# Revit family: HVAC-Chilled_Beam-Dadanco-ACB30
name_source: partatom
category: Mechanical Equipment
revit_build: Autodesk Revit 2015 (Build: 20140903_1530(x64)
units: mm (PartAtom-declared; Revit-internal decimal feet)

## types (6) — shared parameters
Assembly Code = D3040100
Cooling Primary Air Dry Bulb = 55 °F
Cooling Primary Air Wet Bulb = 53 °F
Cooling Room Dry Bulb = 75 °F
Cooling Room Relative Humidity = 50
Default Elevation = 9' - 0"
Description = Active Chilled Beam
Drain material = <By Category>
Heating Primary Air Dry Bulb = 55 °F
Heating Room Dry Bulb = 70 °F
Height = 0' - 11 11/16"
Housing Material = Metal-Dadanco-Steel-Galvanized
Keynote = 23 37 00.A1
Manufacturer = Dadanco
Model = ACB30
SCHW Temperature = 57 °F
SHHW Temperature = 110 °F
Type Comments = 1 Way, Discharge Vertical Coil
URL = http://www.dadanco.com
Width = 0' - 8 25/32"

## per-type parameters (varying)
- ACB-1: 2 Pipe Coil Configuration=No; 2 or 4 pipe=4; CWF=2 GPM; CWPD=3.40 psi; Cooling Supply Air Temperature=58 °F; HWF=1 GPM; HWPD=0.32 psi; Heating Supply Air Temperature=91 °F; Latent Cooling=140.0 Btu/h; Length=2' - 0"; Net Unit Cooling Sensible=1731.0 Btu/h; Net Unit Heating Sensible=2209.0 Btu/h; Nominal Unit Length=2' - 0"; Nozzle Configuration=15-SN; PA=20 CFM; PASP=0.50 in-wg; Primary Air Inlet Size=0' - 4"; SCHW Temp Out=59 °F; SHHW Temp Out=99 °F; Secondary Air Sensible Cooling=1296.0 Btu/h; Secondary Air Sensible Heating=2535.0 Btu/h; Sound Level NC=15; Sound Level dBA=20; Supply Air=96 CFM; Total Cooling Capacity=1870.0 Btu/h
- ACB-2: 2 Pipe Coil Configuration=No; 2 or 4 pipe=4; CWF=1 GPM; CWPD=0.40 psi; Cooling Supply Air Temperature=61 °F; HWF=2 GPM; HWPD=1.08 psi; Heating Supply Air Temperature=87 °F; Latent Cooling=279.0 Btu/h; Length=2' - 8"; Net Unit Cooling Sensible=2427.0 Btu/h; Net Unit Heating Sensible=3071.0 Btu/h; Nominal Unit Length=3' - 0"; Nozzle Configuration=25-MN; PA=40 CFM; PASP=0.40 in-wg; Primary Air Inlet Size=0' - 4"; SCHW Temp Out=64 °F; SHHW Temp Out=105 °F; Secondary Air Sensible Cooling=1558.0 Btu/h; Secondary Air Sensible Heating=3722.0 Btu/h; Sound Level NC=15; Sound Level dBA=22; Supply Air=165 CFM; Total Cooling Capacity=2706.0 Btu/h
- ACB-3: 2 Pipe Coil Configuration=No; 2 or 4 pipe=4; CWF=1 GPM; CWPD=1.90 psi; Cooling Supply Air Temperature=61 °F; HWF=1 GPM; HWPD=0.48 psi; Heating Supply Air Temperature=86 °F; Latent Cooling=349.0 Btu/h; Length=3' - 4"; Net Unit Cooling Sensible=3261.0 Btu/h; Net Unit Heating Sensible=3576.0 Btu/h; Nominal Unit Length=4' - 0"; Nozzle Configuration=35-MN; PA=50 CFM; PASP=0.40 in-wg; Primary Air Inlet Size=0' - 6"; SCHW Temp Out=62 °F; SHHW Temp Out=99 °F; Secondary Air Sensible Cooling=2174.0 Btu/h; Secondary Air Sensible Heating=4391.0 Btu/h; Sound Level NC=16; Sound Level dBA=26; Supply Air=209 CFM; Total Cooling Capacity=3610.0 Btu/h
- ACB-4: 2 Pipe Coil Configuration=Yes; 2 or 4 pipe=2; CWF=1 GPM; CWPD=2.50 psi; Cooling Supply Air Temperature=60 °F; HWF=1 GPM; HWPD=4.56 psi; Heating Supply Air Temperature=92 °F; Latent Cooling=419.0 Btu/h; Length=4' - 4"; Net Unit Cooling Sensible=4351.0 Btu/h; Net Unit Heating Sensible=6173.0 Btu/h; Nominal Unit Length=5' - 0"; Nozzle Configuration=40-MN; PA=60 CFM; PASP=0.40 in-wg; Primary Air Inlet Size=0' - 6"; SCHW Temp Out=65 °F; SHHW Temp Out=97 °F; Secondary Air Sensible Cooling=3048.0 Btu/h; Secondary Air Sensible Heating=7151.0 Btu/h; Sound Level NC=19; Sound Level dBA=30; Supply Air=261 CFM; Total Cooling Capacity=4770.0 Btu/h
- ACB-5: 2 Pipe Coil Configuration=No; 2 or 4 pipe=4; CWF=1 GPM; CWPD=4.20 psi; Cooling Supply Air Temperature=61 °F; HWF=1 GPM; HWPD=1.40 psi; Heating Supply Air Temperature=87 °F; Latent Cooling=489.0 Btu/h; Length=5' - 4"; Net Unit Cooling Sensible=4689.0 Btu/h; Net Unit Heating Sensible=5614.0 Btu/h; Nominal Unit Length=6' - 0"; Nozzle Configuration=45-MN; PA=70 CFM; PASP=0.40 in-wg; Primary Air Inlet Size=0' - 6"; SCHW Temp Out=63 °F; SHHW Temp Out=98 °F; Secondary Air Sensible Cooling=3168.0 Btu/h; Secondary Air Sensible Heating=6755.0 Btu/h; Sound Level NC=21; Sound Level dBA=33; Supply Air=311 CFM; Total Cooling Capacity=5178.0 Btu/h
- ACB-6: 2 Pipe Coil Configuration=No; 2 or 4 pipe=4; CWF=1 GPM; CWPD=1.90 psi; Cooling Supply Air Temperature=61 °F; HWF=1 GPM; HWPD=0.64 psi; Heating Supply Air Temperature=86 °F; Latent Cooling=349.0 Btu/h; Length=3' - 4"; Net Unit Cooling Sensible=3389.0 Btu/h; Net Unit Heating Sensible=3991.0 Btu/h; Nominal Unit Length=4' - 0"; Nozzle Configuration=30-MN; PA=50 CFM; PASP=0.50 in-wg; Primary Air Inlet Size=0' - 6"; SCHW Temp Out=62 °F; SHHW Temp Out=100 °F; Secondary Air Sensible Cooling=2302.0 Btu/h; Secondary Air Sensible Heating=4806.0 Btu/h; Sound Level NC=17; Sound Level dBA=27; Supply Air=223 CFM; Total Cooling Capacity=3738.0 Btu/h

## geometry (parser evidence)
native form markers: Blend x6, Sweep x5
no freeform markers — native parametric forms only
